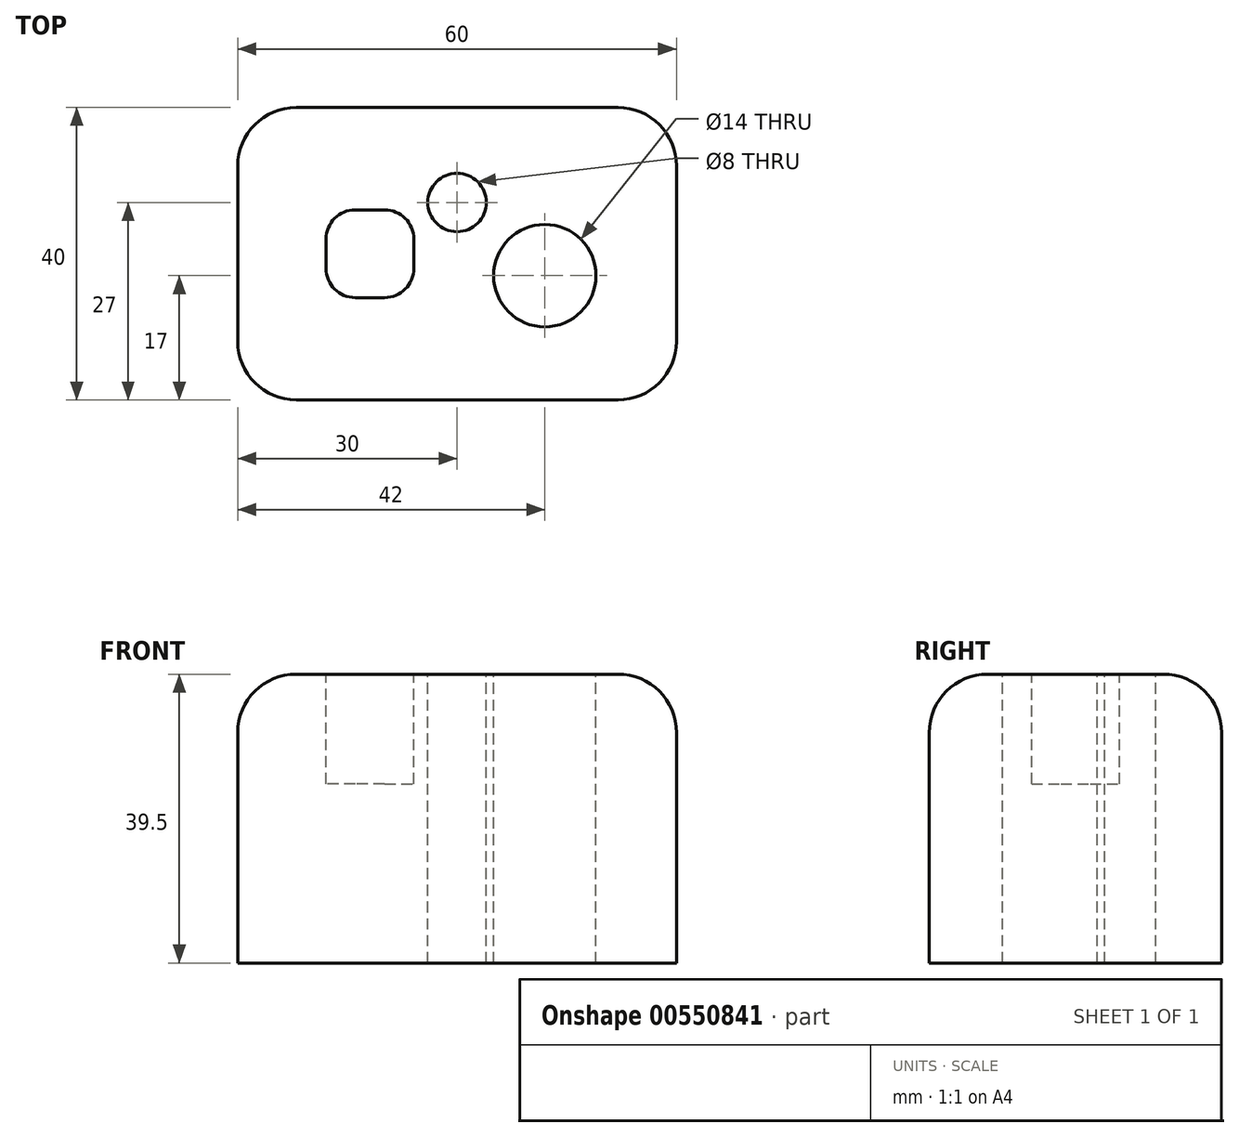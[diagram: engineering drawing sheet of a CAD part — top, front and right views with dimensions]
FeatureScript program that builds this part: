
annotation { "Feature Type Name" : "Feature", "Feature Type Description" : "" }
export const myFeature = defineFeature(function(context is Context, id is Id, definition is map)
    precondition{}
    {
        {
            var Q0;
            Q0=qCreatedBy(makeId("Top.planeOp"),FACE);
            var sketch = newSketch(context, id + "F0", { "sketchPlane" : qUnion([Q0])});
            skLineSegment(sketch, "E0.bottom", {"start": v(0, 0) * mm, "end": v(60, 0) * mm});
            skLineSegment(sketch, "E0.top", {"start": v(0, 40) * mm, "end": v(60, 40) * mm});
            skLineSegment(sketch, "E0.left", {"start": v(0, 0) * mm, "end": v(0, 40) * mm});
            skLineSegment(sketch, "E0.right", {"start": v(60, 0) * mm, "end": v(60, 40) * mm});
            skSolve(sketch);
        }
        {
            var Q0;
            Q0=qSketchRegion(id+"F0",true);
            extrude(context, id + "F1", {"entities" : qUnion([Q0]), "depth" : 39.5 * mm, "offsetDistance" : 25 * mm});
        }
        {
            var Q0;
            Q0=makeQuery(id+"F1.opExtrude","CAP_FACE",FACE,{"disambiguationData":[OSD([sQuery(id+"F0.wireOp",EDGE,"E0.bottom"),sQuery(id+"F0.wireOp",EDGE,"E0.top"),sQuery(id+"F0.wireOp",EDGE,"E0.left"),sQuery(id+"F0.wireOp",EDGE,"E0.right")])],"isStart":false});
            var Q1;
            Q1=makeQuery(id+"F1.opExtrude","SWEPT_EDGE",EDGE,{"disambiguationData":[OSD([sQuery(id+"F0.wireOp",EDGE,"E0.bottom"),sQuery(id+"F0.wireOp",EDGE,"E0.right")])]});
            var Q2;
            Q2=makeQuery(id+"F1.opExtrude","SWEPT_EDGE",EDGE,{"disambiguationData":[OSD([sQuery(id+"F0.wireOp",EDGE,"E0.top"),sQuery(id+"F0.wireOp",EDGE,"E0.right")])]});
            var Q3;
            Q3=makeQuery(id+"F1.opExtrude","SWEPT_EDGE",EDGE,{"disambiguationData":[OSD([sQuery(id+"F0.wireOp",EDGE,"E0.bottom"),sQuery(id+"F0.wireOp",EDGE,"E0.left")])]});
            var Q4;
            Q4=makeQuery(id+"F1.opExtrude","SWEPT_EDGE",EDGE,{"disambiguationData":[OSD([sQuery(id+"F0.wireOp",EDGE,"E0.top"),sQuery(id+"F0.wireOp",EDGE,"E0.left")])]});
            fillet(context, id + "F2", {"entities" : qUnion([Q0, Q1, Q2, Q3, Q4]), "radius" : 8 * mm, "tangentPropagation" : true, "allowEdgeOverflow" : false});
        }
        {
            var Q0;
            Q0=makeQuery(id+"F1.opExtrude","CAP_FACE",FACE,{"disambiguationData":[OSD([sQuery(id+"F0.wireOp",EDGE,"E0.bottom"),sQuery(id+"F0.wireOp",EDGE,"E0.top"),sQuery(id+"F0.wireOp",EDGE,"E0.left"),sQuery(id+"F0.wireOp",EDGE,"E0.right")])],"isStart":false});
            var sketch = newSketch(context, id + "F3", { "sketchPlane" : qUnion([Q0])});
            skLineSegment(sketch, "E1.bottom", {"start": v(24.08, 14) * mm, "end": v(12.08, 14) * mm});
            skLineSegment(sketch, "E1.top", {"start": v(24.08, 26) * mm, "end": v(12.08, 26) * mm});
            skLineSegment(sketch, "E1.left", {"start": v(24.08, 14) * mm, "end": v(24.08, 26) * mm});
            skLineSegment(sketch, "E1.right", {"start": v(12.08, 14) * mm, "end": v(12.08, 26) * mm});
            skPoint(sketch, "E1.middle", {"position": v(18.08, 20) * mm});
            skPoint(sketch, "E1.middle.positionSnap0", {"position": v(8, 20) * mm});
            skPoint(sketch, "E1.centerSnap0", {"position": v(8, 20) * mm});
            skSolve(sketch);
        }
        {
            var Q0;
            Q0=qSketchRegion(id+"F3",true);
            extrude(context, id + "F4", {"entities" : qUnion([Q0]), "operationType" : NewBodyOperationType.REMOVE, "oppositeDirection" : true, "depth" : 15 * mm, "offsetDistance" : 25 * mm});
        }
        {
            var Q0;
            Q0=makeQuery(id+"F4.boolean.opBoolean","COPY",EDGE,{"derivedFrom":makeQuery(id+"F4.opExtrude","SWEPT_EDGE",EDGE,{"disambiguationData":[OSD([sQuery(id+"F3.wireOp",EDGE,"E1.top"),sQuery(id+"F3.wireOp",EDGE,"E1.right")])]})});
            var Q1;
            Q1=makeQuery(id+"F4.boolean.opBoolean","COPY",EDGE,{"derivedFrom":makeQuery(id+"F4.opExtrude","SWEPT_EDGE",EDGE,{"disambiguationData":[OSD([sQuery(id+"F3.wireOp",EDGE,"E1.bottom"),sQuery(id+"F3.wireOp",EDGE,"E1.right")])]})});
            var Q2;
            Q2=makeQuery(id+"F4.boolean.opBoolean","COPY",EDGE,{"derivedFrom":makeQuery(id+"F4.opExtrude","SWEPT_EDGE",EDGE,{"disambiguationData":[OSD([sQuery(id+"F3.wireOp",EDGE,"E1.top"),sQuery(id+"F3.wireOp",EDGE,"E1.left")])]})});
            var Q3;
            Q3=makeQuery(id+"F4.boolean.opBoolean","COPY",EDGE,{"derivedFrom":makeQuery(id+"F4.opExtrude","SWEPT_EDGE",EDGE,{"disambiguationData":[OSD([sQuery(id+"F3.wireOp",EDGE,"E1.bottom"),sQuery(id+"F3.wireOp",EDGE,"E1.left")])]})});
            fillet(context, id + "F5", {"entities" : qUnion([Q0, Q1, Q2, Q3]), "radius" : 4 * mm, "tangentPropagation" : true, "allowEdgeOverflow" : false});
        }
        {
            var Q0;
            Q0=makeQuery(id+"F1.opExtrude","CAP_FACE",FACE,{"disambiguationData":[OSD([sQuery(id+"F0.wireOp",EDGE,"E0.bottom"),sQuery(id+"F0.wireOp",EDGE,"E0.top"),sQuery(id+"F0.wireOp",EDGE,"E0.left"),sQuery(id+"F0.wireOp",EDGE,"E0.right")])],"isStart":false});
            var sketch = newSketch(context, id + "F6", { "sketchPlane" : qUnion([Q0])});
            skCircle(sketch, "E2", {"center": v(30, 27) * mm, "radius": 4 * mm});
            skPoint(sketch, "E2.centerSnap0", {"position": v(30, 32) * mm});
            skCircle(sketch, "E3", {"center": v(42, 17) * mm, "radius": 7 * mm});
            skSolve(sketch);
        }
        {
            var Q0;
            Q0=qSketchRegion(id+"F6",true);
            extrude(context, id + "F7", {"entities" : qUnion([Q0]), "operationType" : NewBodyOperationType.REMOVE, "endBound" : BoundingType.THROUGH_ALL, "oppositeDirection" : true, "depth" : 30 * mm, "offsetDistance" : 25 * mm});
        }
    });
